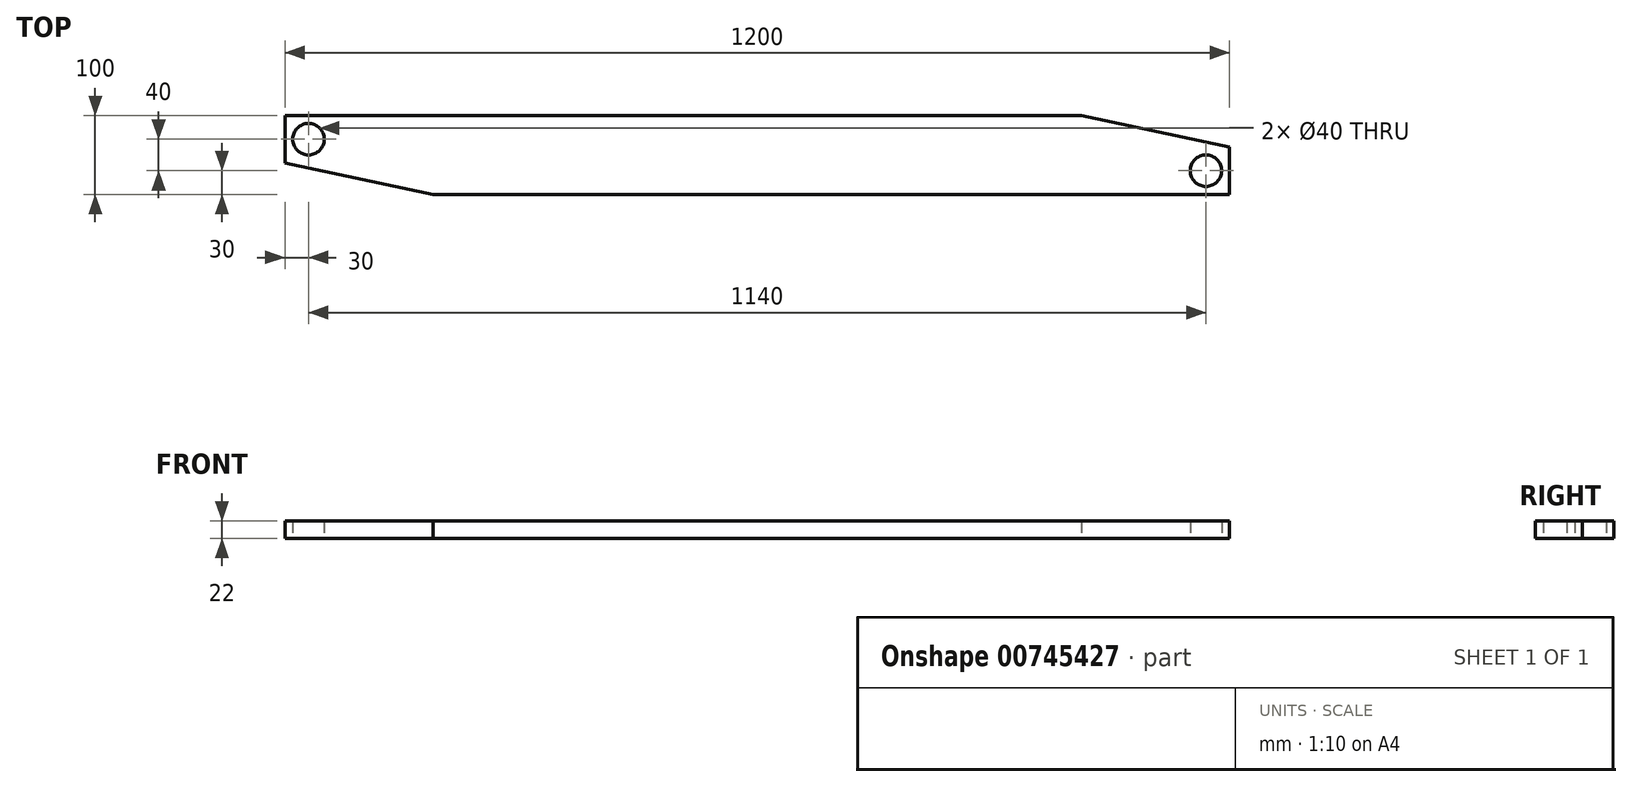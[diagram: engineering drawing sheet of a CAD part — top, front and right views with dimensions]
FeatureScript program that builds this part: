
annotation { "Feature Type Name" : "Feature", "Feature Type Description" : "" }
export const myFeature = defineFeature(function(context is Context, id is Id, definition is map)
    precondition{}
    {
        {
            var Q0;
            Q0=qCreatedBy(makeId("Top.planeOp"),FACE);
            var sketch = newSketch(context, id + "F0", { "sketchPlane" : qUnion([Q0])});
            skLineSegment(sketch, "E0.bottom", {"start": v(-600, 50) * mm, "end": v(411.81, 50) * mm});
            skLineSegment(sketch, "E0.top", {"start": v(-411.81, -50) * mm, "end": v(600, -50) * mm});
            skLineSegment(sketch, "E0.left", {"start": v(-600, 50) * mm, "end": v(-600, -10) * mm});
            skLineSegment(sketch, "E0.right", {"start": v(600, 10) * mm, "end": v(600, -50) * mm});
            skPoint(sketch, "E0.middle", {"position": v(0, 0) * mm});
            skCircle(sketch, "E1", {"center": v(-570, 20) * mm, "radius": 20 * mm});
            skPoint(sketch, "E1.centerSnap0", {"position": v(-600, 0) * mm});
            skLineSegment(sketch, "E2", {"start": v(-600, -10) * mm, "end": v(-411.81, -50) * mm});
            skPoint(sketch, "E3.orphan", {"position": v(-600, -50) * mm});
            skLineSegment(sketch, "E4", {"start": v(411.81, 50) * mm, "end": v(600, 10) * mm});
            skPoint(sketch, "E5.orphan", {"position": v(600, 50) * mm});
            skCircle(sketch, "E6", {"center": v(570, -20) * mm, "radius": 20 * mm});
            skSolve(sketch);
        }
        {
            var Q0;
            Q0 = qSketchRegion(id + "F0", true);
            extrude(context, id + "F1", {"entities" : qUnion([Q0]), "depth" : 22 * mm, "offsetDistance" : 25 * mm});
        }
    });
